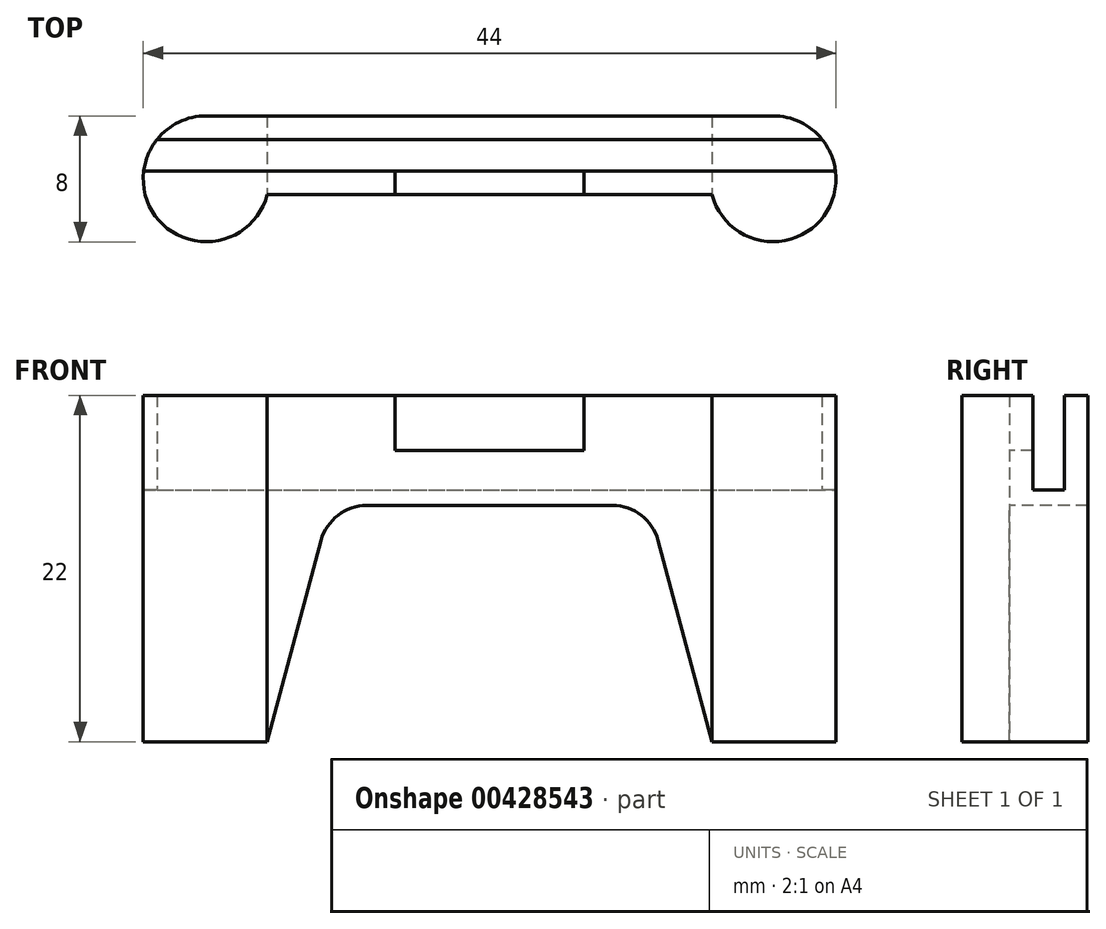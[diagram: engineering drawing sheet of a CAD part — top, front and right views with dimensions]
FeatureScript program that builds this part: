
annotation { "Feature Type Name" : "Feature", "Feature Type Description" : "" }
export const myFeature = defineFeature(function(context is Context, id is Id, definition is map)
    precondition{}
    {
        {
            var Q0;
            Q0=qCreatedBy(makeId("Top.planeOp"),FACE);
            var sketch = newSketch(context, id + "F0", { "sketchPlane" : qUnion([Q0])});
            skCircle(sketch, "E0", {"center": v(0, 0) * mm, "radius": 4 * mm});
            skCircle(sketch, "E1", {"center": v(36, 0) * mm, "radius": 4 * mm});
            skLineSegment(sketch, "E2", {"start": v(0, 0) * mm, "end": v(36, 0) * mm, "construction": true});
            skLineSegment(sketch, "E3.0", {"start": v(0, 4) * mm, "end": v(36, 4) * mm});
            skLineSegment(sketch, "E4", {"start": v(3.87, -1) * mm, "end": v(32.13, -1) * mm});
            skSolve(sketch);
        }
        {
            var Q0;
            Q0 = qSketchRegion(id + "F0", true);
            extrude(context, id + "F1", {"entities" : qUnion([Q0]), "depth" : 22 * mm});
        }
        {
            var Q0;
            Q0=makeQuery(id+"F1.opExtrude","CAP_FACE",FACE,{"disambiguationData":[OSD([sQuery(id+"F0.wireOp",EDGE,"E0"),sQuery(id+"F0.wireOp",EDGE,"E1"),sQuery(id+"F0.wireOp",EDGE,"d0224556-2a80-4e27-880b-63d6de6ceee1.0"),sQuery(id+"F0.wireOp",EDGE,"E3.0")])],"isStart":false});
            var sketch = newSketch(context, id + "F2", { "sketchPlane" : qUnion([Q0])});
            skLineSegment(sketch, "E5.bottom", {"start": v(-4, 2.5) * mm, "end": v(40, 2.5) * mm});
            skLineSegment(sketch, "E5.top", {"start": v(-4, 0.5) * mm, "end": v(40, 0.5) * mm});
            skLineSegment(sketch, "E5.left", {"start": v(-4, 2.5) * mm, "end": v(-4, 0.5) * mm});
            skLineSegment(sketch, "E5.right", {"start": v(40, 2.5) * mm, "end": v(40, 0.5) * mm});
            skLineSegment(sketch, "E6", {"start": v(18, -1) * mm, "end": v(18, 4) * mm, "construction": true});
            skLineSegment(sketch, "E7", {"start": v(-4, 1.5) * mm, "end": v(18, 1.5) * mm, "construction": true});
            skSolve(sketch);
        }
        {
            var Q0;
            Q0 = qSketchRegion(id + "F2", true);
            extrude(context, id + "F3", {"entities" : qUnion([Q0]), "operationType" : NewBodyOperationType.REMOVE, "oppositeDirection" : true, "depth" : 6 * mm});
        }
        {
            var Q0;
            Q0=makeQuery(id+"F1.opExtrude","SWEPT_FACE",FACE,{"disambiguationData":[OSD([sQuery(id+"F0.wireOp",EDGE,"E4")])]});
            var sketch = newSketch(context, id + "F4", { "sketchPlane" : qUnion([Q0])});
            skLineSegment(sketch, "E8", {"start": v(3.87, 0) * mm, "end": v(7.9, 15) * mm});
            skLineSegment(sketch, "E9", {"start": v(7.9, 15) * mm, "end": v(18, 15) * mm});
            skLineSegment(sketch, "E10", {"start": v(18, 15) * mm, "end": v(18, 0) * mm, "construction": true});
            skLineSegment(sketch, "E11.0", {"start": v(3.87, 0) * mm, "end": v(32.13, 0) * mm});
            skLineSegment(sketch, "E12.MirrorCS", {"start": v(28.1, 15) * mm, "end": v(18, 15) * mm});
            skLineSegment(sketch, "E13.MirrorCS", {"start": v(32.13, 0) * mm, "end": v(28.1, 15) * mm});
            skSolve(sketch);
        }
        {
            var Q0;
            Q0 = qSketchRegion(id + "F4", true);
            extrude(context, id + "F5", {"entities" : qUnion([Q0]), "operationType" : NewBodyOperationType.REMOVE, "endBound" : BoundingType.UP_TO_NEXT, "oppositeDirection" : true, "depth" : 25 * mm});
        }
        {
            var Q0;
            Q0=makeQuery(id+"F1.opExtrude","SWEPT_FACE",FACE,{"disambiguationData":[OSD([sQuery(id+"F0.wireOp",EDGE,"E4")])]});
            var sketch = newSketch(context, id + "F6", { "sketchPlane" : qUnion([Q0])});
            skLineSegment(sketch, "E14.bottom", {"start": v(12, 18.5) * mm, "end": v(24, 18.5) * mm});
            skLineSegment(sketch, "E14.top", {"start": v(12, 22) * mm, "end": v(24, 22) * mm});
            skLineSegment(sketch, "E14.left", {"start": v(12, 22) * mm, "end": v(12, 18.5) * mm});
            skLineSegment(sketch, "E14.right", {"start": v(24, 22) * mm, "end": v(24, 18.5) * mm});
            skLineSegment(sketch, "E15", {"start": v(18, 22) * mm, "end": v(18, 18.5) * mm, "construction": true});
            skSolve(sketch);
        }
        {
            var Q0;
            Q0 = qSketchRegion(id + "F6", true);
            extrude(context, id + "F7", {"entities" : qUnion([Q0]), "operationType" : NewBodyOperationType.REMOVE, "oppositeDirection" : true, "depth" : 3.5 * mm});
        }
        {
            var Q0;
            Q0=makeQuery(id+"F5.boolean.opBoolean","COPY",EDGE,{"derivedFrom":makeQuery(id+"F5.opExtrude","SWEPT_EDGE",EDGE,{"disambiguationData":[OSD([sQuery(id+"F4.wireOp",EDGE,"E8"),sQuery(id+"F4.wireOp",EDGE,"E9")])]})});
            var Q1;
            Q1=makeQuery(id+"F5.boolean.opBoolean","COPY",EDGE,{"derivedFrom":makeQuery(id+"F5.opExtrude","SWEPT_EDGE",EDGE,{"disambiguationData":[OSD([sQuery(id+"F4.wireOp",EDGE,"E12.MirrorCS"),sQuery(id+"F4.wireOp",EDGE,"E13.MirrorCS")])]})});
            fillet(context, id + "F8", {"entities" : qUnion([Q0, Q1]), "radius" : 3 * mm, "tangentPropagation" : true, "allowEdgeOverflow" : false});
        }
    });
